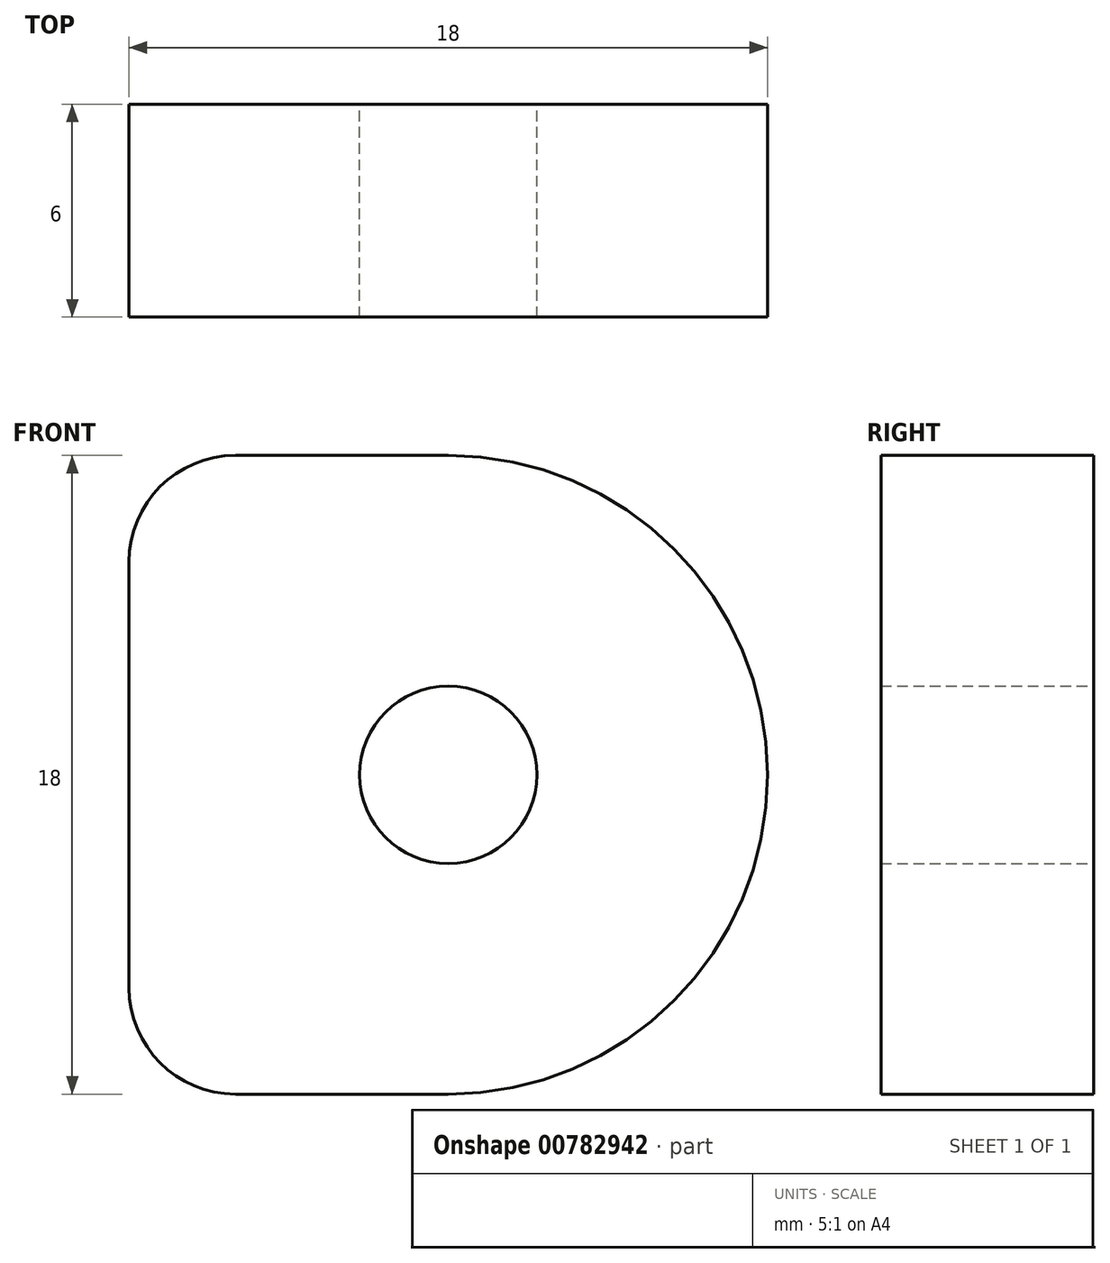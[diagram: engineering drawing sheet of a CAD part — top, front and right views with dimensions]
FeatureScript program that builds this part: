
annotation { "Feature Type Name" : "Feature", "Feature Type Description" : "" }
export const myFeature = defineFeature(function(context is Context, id is Id, definition is map)
    precondition{}
    {
        {
            var Q0;
            Q0=qCreatedBy(makeId("Front.planeOp"),FACE);
            var sketch = newSketch(context, id + "F0", { "sketchPlane" : qUnion([Q0])});
            skLineSegment(sketch, "E0.bottom", {"start": v(0, 0) * mm, "end": v(9, 0) * mm});
            skLineSegment(sketch, "E0.top", {"start": v(0, 18) * mm, "end": v(9, 18) * mm});
            skLineSegment(sketch, "E0.left", {"start": v(0, 0) * mm, "end": v(0, 18) * mm});
            skCircle(sketch, "E1", {"center": v(9, 9) * mm, "radius": 2.5 * mm});
            skPoint(sketch, "E1.centerSnap0", {"position": v(0, 9) * mm});
            skPoint(sketch, "E1.centerSnap1", {"position": v(9, 18) * mm});
            skCircle(sketch, "E2", {"center": v(9, 9) * mm, "radius": 9 * mm});
            skPoint(sketch, "E3.orphan", {"position": v(18, 18) * mm});
            skSolve(sketch);
        }
        {
            var Q0;
            Q0=qSketchRegion(id+"F0",true);
            extrude(context, id + "F1", {"entities" : qUnion([Q0]), "depth" : 6 * mm, "offsetDistance" : 25 * mm});
        }
        {
            var Q0;
            Q0=makeQuery(id+"F1.opExtrude","SWEPT_EDGE",EDGE,{"disambiguationData":[OSD([sQuery(id+"F0.wireOp",EDGE,"E0.bottom"),sQuery(id+"F0.wireOp",EDGE,"E0.right")])]});
            var Q1;
            Q1=makeQuery(id+"F1.opExtrude","SWEPT_EDGE",EDGE,{"disambiguationData":[OSD([sQuery(id+"F0.wireOp",EDGE,"E0.top"),sQuery(id+"F0.wireOp",EDGE,"E0.right")])]});
            var Q2;
            Q2=makeQuery(id+"F1.opExtrude","SWEPT_EDGE",EDGE,{"disambiguationData":[OSD([sQuery(id+"F0.wireOp",EDGE,"E0.top"),sQuery(id+"F0.wireOp",EDGE,"E0.left")])]});
            var Q3;
            Q3=makeQuery(id+"F1.opExtrude","SWEPT_EDGE",EDGE,{"disambiguationData":[OSD([sQuery(id+"F0.wireOp",EDGE,"E0.bottom"),sQuery(id+"F0.wireOp",EDGE,"E0.left")])]});
            fillet(context, id + "F2", {"entities" : qUnion([Q0, Q1, Q2, Q3]), "radius" : 3 * mm, "tangentPropagation" : true, "allowEdgeOverflow" : false});
        }
    });
